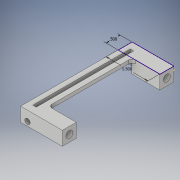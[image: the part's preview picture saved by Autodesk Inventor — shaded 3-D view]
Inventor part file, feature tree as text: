
AUTODESK INVENTOR PART (.ipt)
format: ipt  version: 2018 (Build 220112000, 112)  size: 167,936 bytes
history: native  units: in
note: dims shown in document units (in); Inventor stores cm internally (conversion verified against a paired STEP export)
features: sketch x10, extrude x6, hole x2, fillet x1
ambient origin geometry x8: Origin, YZ Plane, XZ Plane, XY Plane, X Axis, Y Axis, Z Axis, Center Point
bodies: Solid1 (feature_tree)
feature tree (19):
  sketch  "Sketch1"  dims[d0=1.5in d1=0.5in]
  extrude  "Extrusion1"  Depth=0.5in
  extrude  "Extrusion2"  Depth=0.5in
  extrude  "Extrusion3"  Depth=0.5in
  sketch  "Sketch5"  dims[d10=4.0in d11=0.125in d12=0.0in d13=0.5in d14=0.0in]
  extrude  "Extrusion4"  Depth=0.25in TaperAngle=0.0deg
  extrude  "Extrusion5"  Depth=0.125in TaperAngle=0.0deg
  fillet  "Fillet1"  Radius=0.5in
  hole  "Hole1"  [1 undecoded]
  extrude  "Extrusion6"  Depth=0.125in
  hole  "Hole2"  [1 undecoded]
  sketch  "Sketch2"  dims[d2=1.0in d3=0.5in]
  sketch  "Sketch3"  dims[d4=0.5in d5=0.0in d6=0.5in]
  sketch  "Sketch4"  dims[d7=0.5in d8=0.25in d9=0.0in]
  sketch  "Sketch6"  dims[d15=0.25in d16=0.0in d17=0.125in]
  sketch  "Sketch7"  dims[d18=0.19in d19=0.75in d20=0.375in d21=0.25in d22=0.5635in d23=4.25in d24=0.8108in d25=0.125in]
  sketch  "Sketch8"  dims[d26=3.5in d27=0.25in d28=0.0in]
  sketch  "Sketch9"  dims[d29=0.25in d30=0.75in d31=0.375in d32=0.25in d33=0.5635in d34=0.5in d35=0.8108in]
  sketch  "Sketch10"
note: 2 required parameter values undecoded (feature->parameter linkage not recoverable at this tier; creation-order binding heuristic only, values carry confidence <= 0.55)
